# Revit family: DO_WPB_Dynamicroll-Cleanroom_BMP
name_source: partatom
category: Doors
units: mm (PartAtom-declared; Revit-internal decimal feet)

## family parameters
Always vertical = Yes
Cut with Voids When Loaded = Yes
OmniClass Number = 23.17.11.45.17
Room Calculation Point = No
Shared = No
Work Plane-Based = Yes

## types (2) — shared parameters
Analytic Construction = <None>
Classification.OmniClass.23.Description = Rapid Opening Doors
Classification.OmniClass.23.Number = 23.17.11.45.17
Classification.Uniclass.EF.Description = Doors
Classification.Uniclass.EF.Number = EF_25_30_25
Classification.Uniclass.Pr.Description = High-speed doorsets
Classification.Uniclass.Pr.Number = Pr_30_59_24_38
Classification.Uniclass.Ss.Description = High-speed doorset systems
Classification.Uniclass.Ss.Number = Ss_25_30_20_38
Define Thermal Properties by = Schematic Type
Description = High Speed Door
IfcDescription = High Speed Door
IfcExportAs = IfcDoor
IfcExportType = DOOR
LOD300 = No
LOD400 = Yes
Manufacturer = BMP High Speed Doors
RSen_C_clashvolume = No
RSen_C_code_ETIM = EC003229
RSen_C_code_ETIM_url = https://prod.etim-international.com
RSen_C_content_modification_date = 2025.01.22
RSen_C_content_provider = BMP High Speed Doors
RSen_C_content_version = V2
csv = Dynamicroll Cleanroom
csv_metadata = Dynamicroll Cleanroom_data
curtain_bottom_height = 120 mm  [stored 0.393701 ft]
curtain_bottom_material = Plastic, black
curtain_material = PVC
do_type0 = curtain : panel
do_type1 = curtain : rectangle window
do_type2 = curtain : full width window
do_type3 = curtain : full vision window
do_type4 = curtain : rounded corner window
ee_type1 = EE_WPB_control panel_BMP_SH : Control panel SS304
ee_type2 = EE_WPB_control panel_BMP_SH : Control panel PVC
ee_type4 = EE_WPB_control panel_BMP_SH : Control panel Powder coated steel
frame_material = Steel, galvanized
motor_cover_material = Steel, galvanized
region_index = 44
si_type0 = window type : No windows
si_type1 = window type : Rectangle window
si_type2 = window type : Full width window
si_type3 = window type : Full vision window
si_type4 = window type : Rounded corner window
si_type5 = curtain type : Standard curtain
si_type6 = curtain type : Insulated curtain 7mm
si_type7 = curtain type : FDA approved curtain
si_type8 = curtain type : Antistatic curtain
si_type9 = curtain type : Translucent curtain
window_material = Glass, transparent
zero-valued in all types: Default Elevation

## per-type parameters (varying)
| type | Model | RSen_C_model | type_index |
| CB125 | Dynamicroll CB125 | Dynamicroll CB125 | 1 |
| CB230 | Dynamicroll CB230 | Dynamicroll CB230 | 2 |

note: [stored X ft] marks values corroborated as IEEE doubles in the binary element streams (Revit-internal decimal feet)

## geometry (parser evidence)
native form markers: Sweep x29
no freeform markers — native parametric forms only
